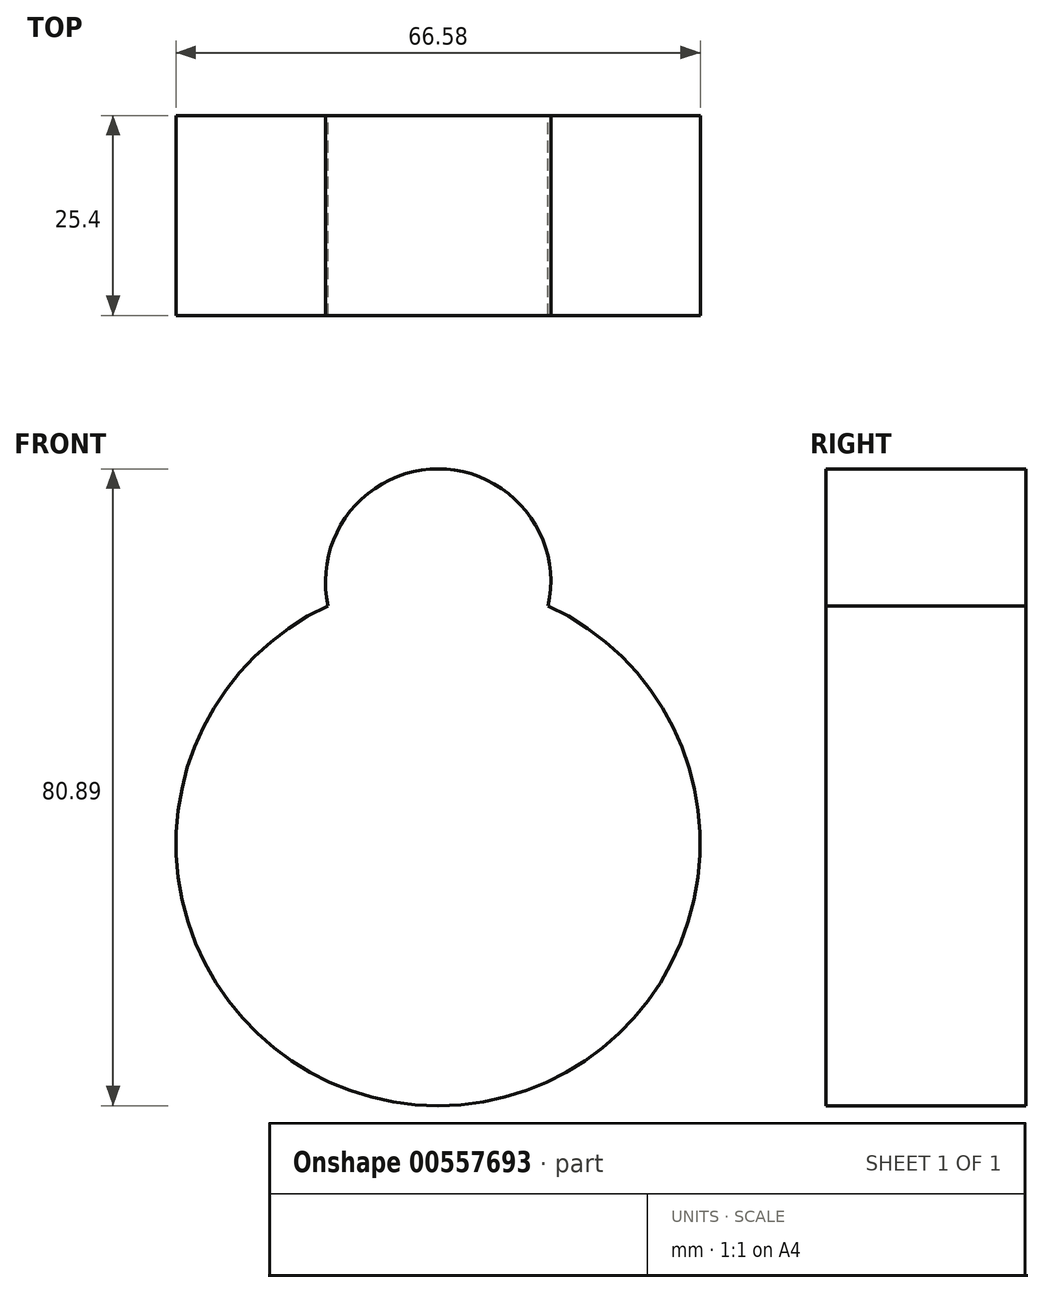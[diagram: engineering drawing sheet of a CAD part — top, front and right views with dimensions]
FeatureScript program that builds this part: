
annotation { "Feature Type Name" : "Feature", "Feature Type Description" : "" }
export const myFeature = defineFeature(function(context is Context, id is Id, definition is map)
    precondition{}
    {
        {
            var Q0;
            Q0=qCreatedBy(makeId("Front.planeOp"),FACE);
            var sketch = newSketch(context, id + "F0", { "sketchPlane" : qUnion([Q0])});
            skArc(sketch, "E0", {"start": v(-13.97, 30.21) * mm, "mid": v(0, -33.29) * mm, "end": v(13.97, 30.21) * mm});
            skArc(sketch, "E1", {"start": v(13.97, 30.21) * mm, "mid": v(0, 47.6) * mm, "end": v(-13.97, 30.21) * mm});
            skSolve(sketch);
        }
        {
            var Q0;
            Q0 = qSketchRegion(id + "F0", true);
            extrude(context, id + "F1", {"entities" : qUnion([Q0]), "depth" : 25.4 * mm, "offsetDistance" : 25.4 * mm});
        }
    });
